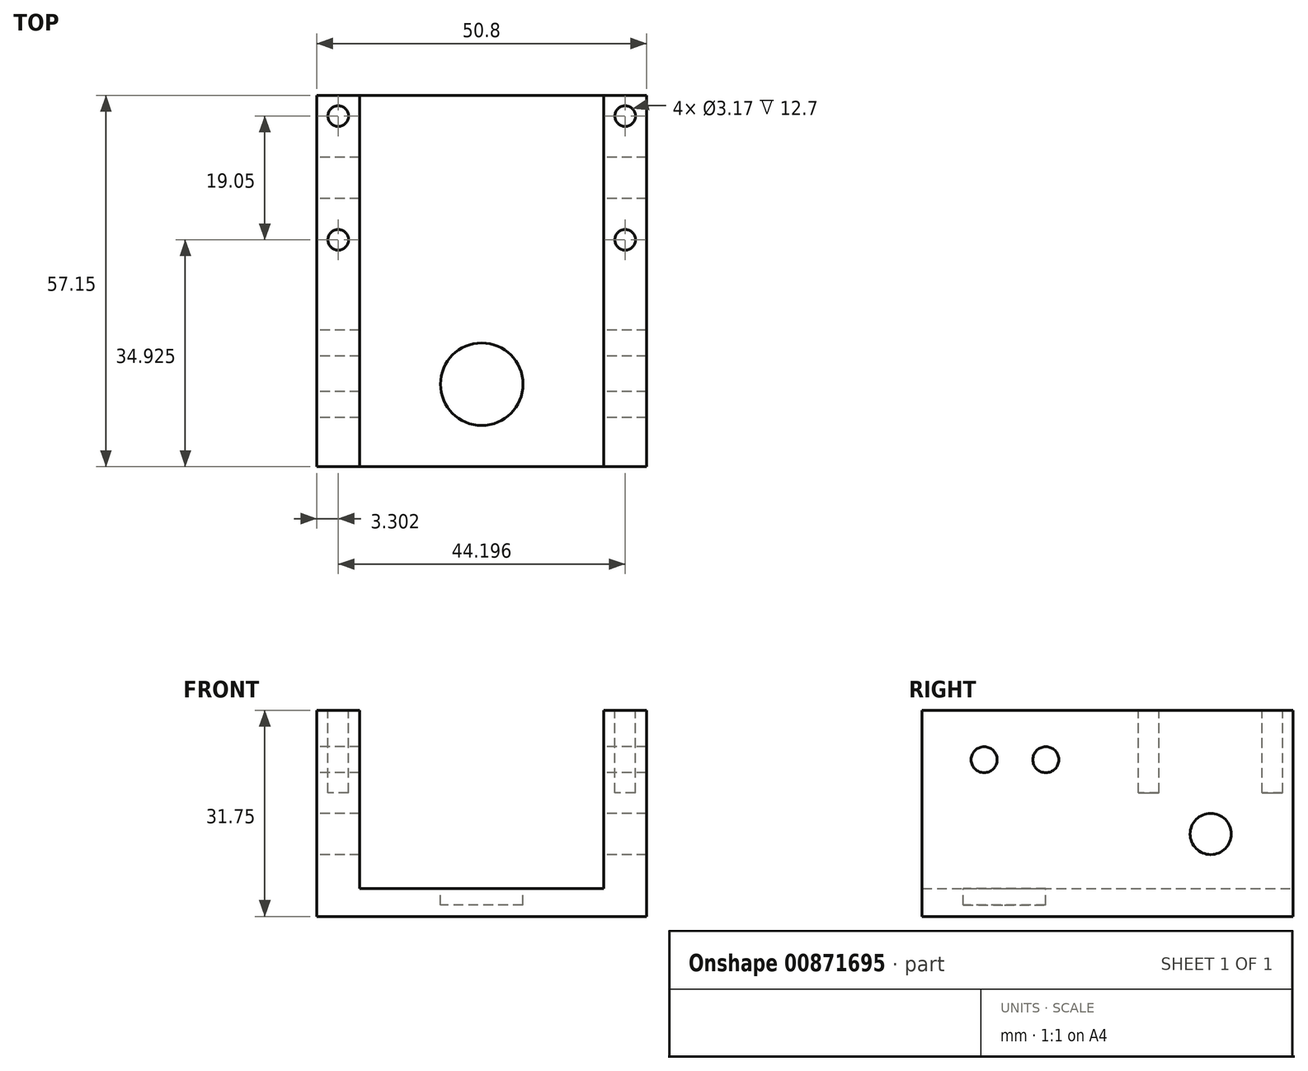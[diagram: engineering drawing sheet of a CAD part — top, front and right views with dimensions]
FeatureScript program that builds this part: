
annotation { "Feature Type Name" : "Feature", "Feature Type Description" : "" }
export const myFeature = defineFeature(function(context is Context, id is Id, definition is map)
    precondition{}
    {
        {
            var Q0;
            Q0=qCreatedBy(makeId("Front.planeOp"),FACE);
            var sketch = newSketch(context, id + "F0", { "sketchPlane" : qUnion([Q0])});
            skLineSegment(sketch, "E0", {"start": v(0, 0) * mm, "end": v(25.4, 0) * mm});
            skLineSegment(sketch, "E1", {"start": v(25.4, 0) * mm, "end": v(25.4, 31.75) * mm});
            skLineSegment(sketch, "E2", {"start": v(25.4, 31.75) * mm, "end": v(18.8, 31.75) * mm});
            skLineSegment(sketch, "E3", {"start": v(18.8, 31.75) * mm, "end": v(18.8, 4.32) * mm});
            skLineSegment(sketch, "E4", {"start": v(18.8, 4.32) * mm, "end": v(0, 4.32) * mm});
            skLineSegment(sketch, "E5.MirrorCS", {"start": v(-18.8, 4.32) * mm, "end": v(0, 4.32) * mm});
            skLineSegment(sketch, "E6.MirrorCS", {"start": v(-18.8, 31.75) * mm, "end": v(-18.8, 4.32) * mm});
            skLineSegment(sketch, "E7.MirrorCS", {"start": v(-25.4, 31.75) * mm, "end": v(-18.8, 31.75) * mm});
            skLineSegment(sketch, "E8.MirrorCS", {"start": v(-25.4, 0) * mm, "end": v(-25.4, 31.75) * mm});
            skLineSegment(sketch, "E9.MirrorCS", {"start": v(0, 0) * mm, "end": v(-25.4, 0) * mm});
            skSolve(sketch);
        }
        {
            var Q0;
            Q0 = qSketchRegion(id + "F0", true);
            extrude(context, id + "F1", {"entities" : qUnion([Q0]), "depth" : 57.15 * mm, "offsetDistance" : 25.4 * mm});
        }
        {
            var Q0;
            Q0=makeQuery(id+"F1.opExtrude","SWEPT_FACE",FACE,{"disambiguationData":[OSD([sQuery(id+"F0.wireOp",EDGE,"E8.MirrorCS")])]});
            var sketch = newSketch(context, id + "F2", { "sketchPlane" : qUnion([Q0])});
            skCircle(sketch, "E10", {"center": v(12.7, 12.7) * mm, "radius": 3.18 * mm});
            skSolve(sketch);
        }
        {
            var Q0;
            Q0 = qSketchRegion(id + "F2", true);
            extrude(context, id + "F3", {"entities" : qUnion([Q0]), "operationType" : NewBodyOperationType.REMOVE, "endBound" : BoundingType.THROUGH_ALL, "oppositeDirection" : true, "depth" : 25.4 * mm, "offsetDistance" : 25.4 * mm});
        }
        {
            var Q0;
            Q0=makeQuery(id+"F1.opExtrude","SWEPT_FACE",FACE,{"disambiguationData":[OSD([sQuery(id+"F0.wireOp",EDGE,"E4"),sQuery(id+"F0.wireOp",EDGE,"E5.MirrorCS")])]});
            var sketch = newSketch(context, id + "F4", { "sketchPlane" : qUnion([Q0])});
            skCircle(sketch, "E11", {"center": v(0, -44.45) * mm, "radius": 6.35 * mm});
            skSolve(sketch);
        }
        {
            var Q0;
            Q0 = qSketchRegion(id + "F4", true);
            extrude(context, id + "F5", {"entities" : qUnion([Q0]), "operationType" : NewBodyOperationType.REMOVE, "oppositeDirection" : true, "depth" : 2.54 * mm, "offsetDistance" : 25.4 * mm});
        }
        {
            var Q0;
            Q0=makeQuery(id+"F1.opExtrude","SWEPT_FACE",FACE,{"disambiguationData":[OSD([sQuery(id+"F0.wireOp",EDGE,"E8.MirrorCS")])]});
            var sketch = newSketch(context, id + "F6", { "sketchPlane" : qUnion([Q0])});
            skCircle(sketch, "E12", {"center": v(38.1, 24.13) * mm, "radius": 2 * mm});
            skCircle(sketch, "E13", {"center": v(47.6, 24.13) * mm, "radius": 2 * mm});
            skSolve(sketch);
        }
        {
            var Q0;
            Q0 = qSketchRegion(id + "F6", true);
            extrude(context, id + "F7", {"entities" : qUnion([Q0]), "operationType" : NewBodyOperationType.REMOVE, "endBound" : BoundingType.THROUGH_ALL, "oppositeDirection" : true, "depth" : 25.4 * mm, "offsetDistance" : 25.4 * mm});
        }
        {
            var Q0;
            Q0=makeQuery(id+"F1.opExtrude","SWEPT_FACE",FACE,{"disambiguationData":[OSD([sQuery(id+"F0.wireOp",EDGE,"E7.MirrorCS")])]});
            var sketch = newSketch(context, id + "F8", { "sketchPlane" : qUnion([Q0])});
            skCircle(sketch, "E14", {"center": v(-22.1, -3.18) * mm, "radius": 1.59 * mm});
            skCircle(sketch, "E15", {"center": v(-22.1, -22.23) * mm, "radius": 1.59 * mm});
            skCircle(sketch, "E16.MirrorC", {"center": v(22.1, -3.18) * mm, "radius": 1.59 * mm});
            skCircle(sketch, "E17.MirrorC", {"center": v(22.1, -22.23) * mm, "radius": 1.59 * mm});
            skSolve(sketch);
        }
        {
            var Q0;
            Q0 = qSketchRegion(id + "F8", true);
            extrude(context, id + "F9", {"entities" : qUnion([Q0]), "operationType" : NewBodyOperationType.REMOVE, "oppositeDirection" : true, "depth" : 12.7 * mm, "offsetDistance" : 25.4 * mm});
        }
    });
